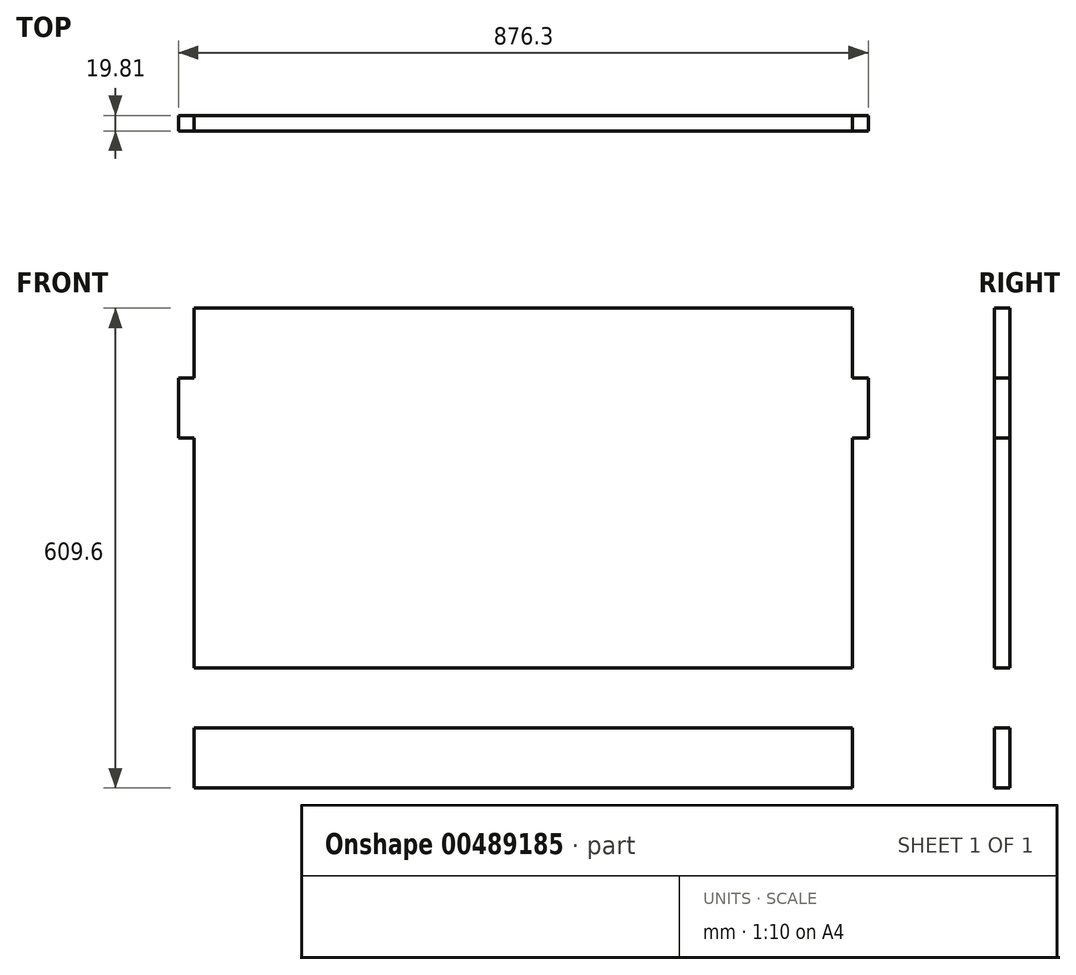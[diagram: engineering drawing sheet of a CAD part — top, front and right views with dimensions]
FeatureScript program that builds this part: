
annotation { "Feature Type Name" : "Feature", "Feature Type Description" : "" }
export const myFeature = defineFeature(function(context is Context, id is Id, definition is map)
    precondition{}
    {
        {
            var Q0;
            Q0=qCreatedBy(makeId("Right.planeOp"),FACE);
            var sketch = newSketch(context, id + "F0", { "sketchPlane" : qUnion([Q0])});
            skLineSegment(sketch, "E0", {"start": v(-65.13, -15.86) * mm, "end": v(-45.32, -15.86) * mm});
            skLineSegment(sketch, "E1", {"start": v(-45.32, -15.86) * mm, "end": v(-45.32, 593.74) * mm});
            skLineSegment(sketch, "E2", {"start": v(-45.32, 593.74) * mm, "end": v(-65.13, 593.74) * mm});
            skLineSegment(sketch, "E3", {"start": v(-65.13, 593.74) * mm, "end": v(-65.13, -15.86) * mm});
            skLineSegment(sketch, "E4", {"start": v(-45.32, 504.84) * mm, "end": v(-65.13, 504.84) * mm});
            skLineSegment(sketch, "E5", {"start": v(-65.13, 504.84) * mm, "end": v(-65.13, 428.64) * mm});
            skLineSegment(sketch, "E6", {"start": v(-65.13, 428.64) * mm, "end": v(-45.32, 428.64) * mm});
            skLineSegment(sketch, "E7", {"start": v(-45.32, 428.64) * mm, "end": v(-45.32, 504.84) * mm});
            skLineSegment(sketch, "E8", {"start": v(-65.13, 60.34) * mm, "end": v(-65.13, 136.54) * mm});
            skLineSegment(sketch, "E9", {"start": v(-65.13, 136.54) * mm, "end": v(-45.32, 136.54) * mm});
            skLineSegment(sketch, "E10", {"start": v(-45.32, 136.54) * mm, "end": v(-45.32, 60.34) * mm});
            skLineSegment(sketch, "E11", {"start": v(-45.32, 60.34) * mm, "end": v(-65.13, 60.34) * mm});
            skSolve(sketch);
        }
        {
            var Q0;
            Q0=makeQuery(id+"F0.imprint","IMPRINT",FACE,{"disambiguationData":[TD([[makeQuery(id+"F0.imprint","IMPRINT",EDGE,{"derivedFrom":sQuery(id+"F0.wireOp",EDGE,"E8")}),-1.0]])]});
            var Q1;
            Q1=makeQuery(id+"F0.imprint","IMPRINT",FACE,{"disambiguationData":[TD([[makeQuery(id+"F0.imprint","IMPRINT",EDGE,{"derivedFrom":sQuery(id+"F0.wireOp",EDGE,"E4")}),1.0]])]});
            var Q2;
            {var subQ0=sQuery(id+"F0.wireOp",EDGE,"E2");Q2=makeQuery(id+"F0.imprint","IMPRINT",FACE,{"disambiguationData":[TD([[makeQuery(id+"F0.imprint","IMPRINT",EDGE,{"derivedFrom":subQ0}),1.0]])]});}
            var Q3;
            {var subQ0=sQuery(id+"F0.wireOp",EDGE,"E6");Q3=makeQuery(id+"F0.imprint","IMPRINT",FACE,{"disambiguationData":[TD([[makeQuery(id+"F0.imprint","IMPRINT",EDGE,{"derivedFrom":subQ0}),-1.0]])]});}
            var Q4;
            {var subQ0=sQuery(id+"F0.wireOp",EDGE,"E0");Q4=makeQuery(id+"F0.imprint","IMPRINT",FACE,{"disambiguationData":[TD([[makeQuery(id+"F0.imprint","IMPRINT",EDGE,{"derivedFrom":subQ0}),1.0]])]});}
            extrude(context, id + "F1", {"entities" : qUnion([Q0, Q1, Q2, Q3, Q4]), "depth" : 836.68 * mm, "offsetDistance" : 25.4 * mm});
        }
        {
            var Q0;
            Q0=makeQuery(id+"F0.imprint","IMPRINT",FACE,{"disambiguationData":[TD([[makeQuery(id+"F0.imprint","IMPRINT",EDGE,{"derivedFrom":sQuery(id+"F0.wireOp",EDGE,"E4")}),1.0]])]});
            var Q1;
            Q1=makeQuery(id+"F0.imprint","IMPRINT",FACE,{"disambiguationData":[TD([[makeQuery(id+"F0.imprint","IMPRINT",EDGE,{"derivedFrom":sQuery(id+"F0.wireOp",EDGE,"E8")}),-1.0]])]});
            extrude(context, id + "F2", {"entities" : qUnion([Q0, Q1]), "operationType" : NewBodyOperationType.ADD, "oppositeDirection" : true, "depth" : 19.8 * mm, "offsetDistance" : 25.4 * mm, "hasSecondDirection" : true, "secondDirectionOppositeDirection" : false, "secondDirectionDepth" : 856.5 * mm});
        }
    });
